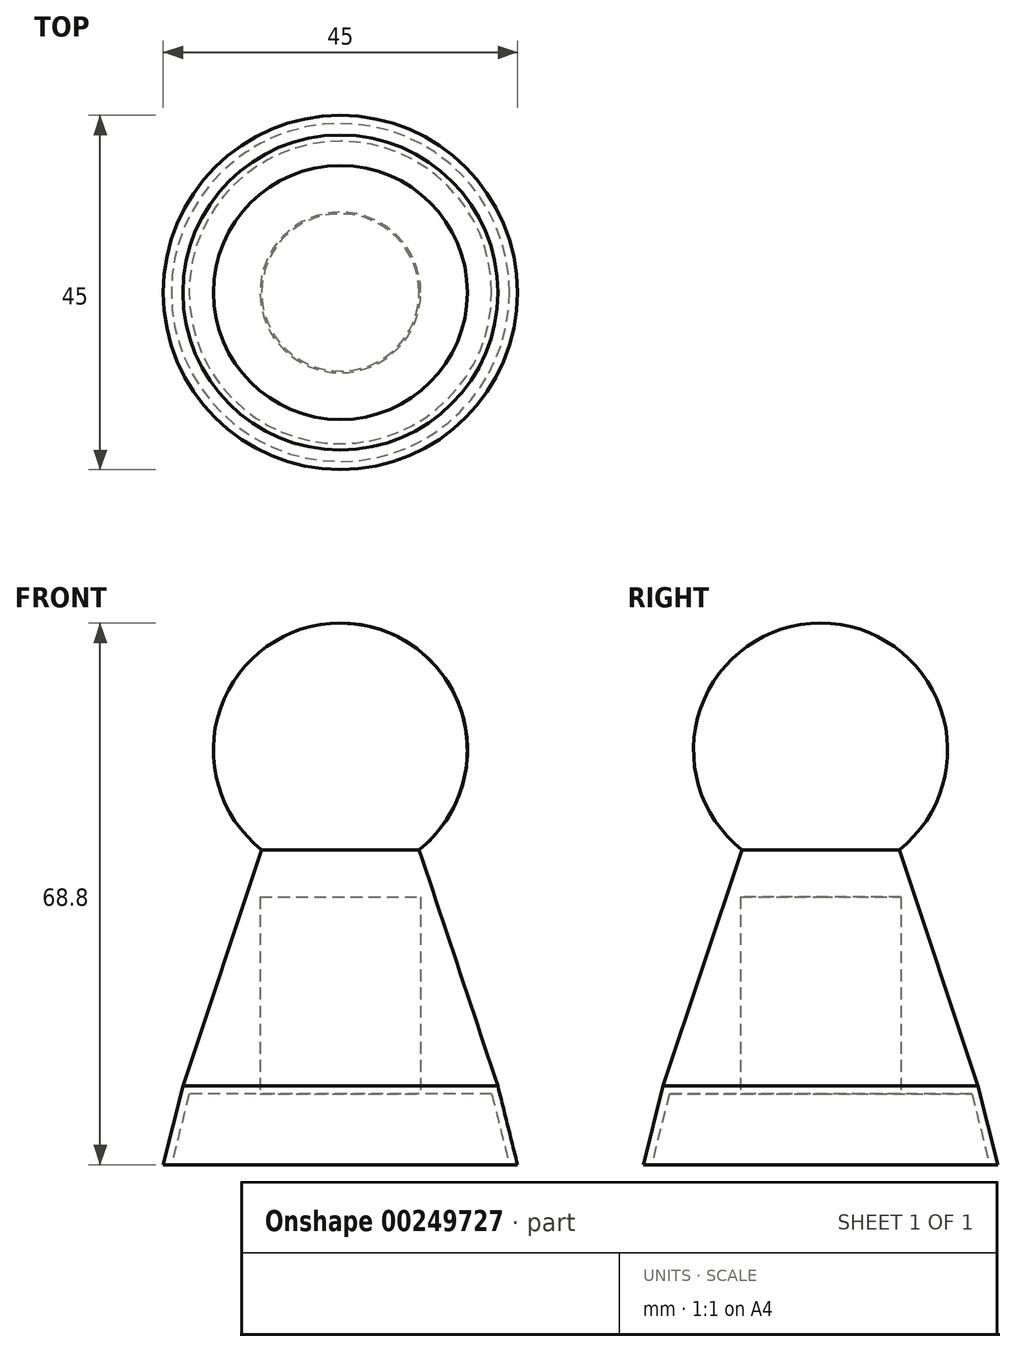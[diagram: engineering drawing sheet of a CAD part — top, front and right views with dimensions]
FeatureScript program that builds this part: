
annotation { "Feature Type Name" : "Feature", "Feature Type Description" : "" }
export const myFeature = defineFeature(function(context is Context, id is Id, definition is map)
    precondition{}
    {
        {
            var Q0;
            Q0=qCreatedBy(makeId("Top.planeOp"),FACE);
            var sketch = newSketch(context, id + "F0", { "sketchPlane" : qUnion([Q0])});
            skCircle(sketch, "E0", {"center": v(0, 0) * mm, "radius": 22.5 * mm});
            skSolve(sketch);
        }
        {
            var Q0;
            Q0=qCreatedBy(makeId("Top.planeOp"),FACE);
            cPlane(context, id + "F1", {"entities" : qUnion([Q0]), "cplaneType" : CPlaneType.OFFSET, "offset" : 10 * mm, "width" : 150 * mm, "height" : 150 * mm});
        }
        {
            var Q0;
            Q0=qCreatedBy(id+"F1.planeOp",FACE);
            var sketch = newSketch(context, id + "F2", { "sketchPlane" : qUnion([Q0])});
            skCircle(sketch, "E1", {"center": v(0, 0) * mm, "radius": 20 * mm});
            skSolve(sketch);
        }
        {
            var Q0;
            Q0=makeQuery(id+"F2.imprint","IMPRINT",FACE,{"disambiguationData":[TD([[makeQuery(id+"F2.imprint","IMPRINT",EDGE,{"derivedFrom":sQuery(id+"F2.wireOp",EDGE,"E1")}),1.0]])]});
            var Q1;
            Q1=makeQuery(id+"F0.imprint","IMPRINT",FACE,{"disambiguationData":[TD([[makeQuery(id+"F0.imprint","IMPRINT",EDGE,{"derivedFrom":sQuery(id+"F0.wireOp",EDGE,"E0")}),1.0]])]});
            loft(context, id + "F3", {"sheetProfilesArray" : [{ "sheetProfileEntities" : qUnion([Q0]) }, { "sheetProfileEntities" : qUnion([Q1]) }]});
        }
        {
            var Q0;
            Q0=makeQuery(id+"F3.opLoft","CAP_FACE",FACE,{"disambiguationData":[OSD([makeQuery(id+"F0.imprint","IMPRINT",FACE,{"disambiguationData":[TD([[makeQuery(id+"F0.imprint","IMPRINT",EDGE,{"derivedFrom":sQuery(id+"F0.wireOp",EDGE,"E0")}),1.0]])]})])],"isStart":true});
            shell(context, id + "F4", {"entities" : qUnion([Q0]), "thickness" : 1 * mm});
        }
        {
            var Q0;
            Q0=makeQuery(id+"F3.opLoft","CAP_FACE",FACE,{"disambiguationData":[OSD([makeQuery(id+"F2.imprint","IMPRINT",FACE,{"disambiguationData":[TD([[makeQuery(id+"F2.imprint","IMPRINT",EDGE,{"derivedFrom":sQuery(id+"F2.wireOp",EDGE,"E1")}),1.0]])]})])],"isStart":true});
            var sketch = newSketch(context, id + "F5", { "sketchPlane" : qUnion([Q0])});
            skSolve(sketch);
        }
        {
            var Q0;
            Q0=makeQuery(id+"F5.imprint","IMPRINT",FACE,{"disambiguationData":[TD([[makeQuery(id+"F5.imprint","IMPRINT",EDGE,{"derivedFrom":makeQuery(id+"F3.opLoft","MID_CAP_EDGE",EDGE,{"disambiguationData":[OSD([sQuery(id+"F2.wireOp",EDGE,"E1")])],"capPos":0.0})}),-1.0]])]});
            cPlane(context, id + "F6", {"entities" : qUnion([Q0]), "cplaneType" : CPlaneType.OFFSET, "offset" : 30 * mm, "width" : 150 * mm, "height" : 150 * mm});
        }
        {
            var Q0;
            Q0=qCreatedBy(id+"F6.planeOp",FACE);
            var sketch = newSketch(context, id + "F7", { "sketchPlane" : qUnion([Q0])});
            skCircle(sketch, "E2", {"center": v(0, 0) * mm, "radius": 10 * mm});
            skSolve(sketch);
        }
        {
            var Q1;
            Q1=makeQuery(id+"F5.imprint","IMPRINT",FACE,{"disambiguationData":[TD([[makeQuery(id+"F5.imprint","IMPRINT",EDGE,{"derivedFrom":makeQuery(id+"F3.opLoft","MID_CAP_EDGE",EDGE,{"disambiguationData":[OSD([sQuery(id+"F2.wireOp",EDGE,"E1")])],"capPos":0.0})}),-1.0]])]});
            var Q2;
            Q2=makeQuery(id+"F7.imprint","IMPRINT",FACE,{"disambiguationData":[TD([[makeQuery(id+"F7.imprint","IMPRINT",EDGE,{"derivedFrom":sQuery(id+"F7.wireOp",EDGE,"E2")}),1.0]])]});
            loft(context, id + "F8", {"operationType" : NewBodyOperationType.ADD, "sheetProfilesArray" : [{ "sheetProfileEntities" : qUnion([Q1]) }, { "sheetProfileEntities" : qUnion([Q2]) }]});
        }
        {
            var Q0;
            Q0=makeQuery(id+"F4.opShell","OFFSET_FACE",FACE,{"disambiguationData":[OSD([makeQuery(id+"F2.imprint","IMPRINT",FACE,{"disambiguationData":[TD([[makeQuery(id+"F2.imprint","IMPRINT",EDGE,{"derivedFrom":sQuery(id+"F2.wireOp",EDGE,"E1")}),1.0]])]})])]});
            var sketch = newSketch(context, id + "F9", { "sketchPlane" : qUnion([Q0])});
            skCircle(sketch, "E3.0.0", {"center": v(0, 0) * mm, "radius": 19.22 * mm, "construction": true});
            skCircle(sketch, "E4", {"center": v(0, 0) * mm, "radius": 10.2 * mm});
            skSolve(sketch);
        }
        {
            var Q0;
            Q0=makeQuery(id+"F9.imprint","IMPRINT",FACE,{"disambiguationData":[TD([[makeQuery(id+"F9.imprint","IMPRINT",EDGE,{"derivedFrom":sQuery(id+"F9.wireOp",EDGE,"E4")}),1.0]])]});
            extrude(context, id + "F10", {"entities" : qUnion([Q0]), "operationType" : NewBodyOperationType.REMOVE, "oppositeDirection" : true, "depth" : 25 * mm});
        }
        {
            var Q0;
            Q0=qCreatedBy(makeId("Front.planeOp"),FACE);
            var sketch = newSketch(context, id + "F11", { "sketchPlane" : qUnion([Q0])});
            skLineSegment(sketch, "E5.0", {"start": v(-10, 40) * mm, "end": v(10, 40) * mm});
            skLineSegment(sketch, "E6", {"start": v(0, 73.64) * mm, "end": v(0, 40) * mm});
            skArc(sketch, "E7", {"start": v(10, 40) * mm, "mid": v(15.24, 57.96) * mm, "end": v(0, 68.8) * mm});
            skSolve(sketch);
        }
        {
            var Q0;
            Q0 = qSketchRegion(id + "F11", true);
            var Q1;
            Q1=sQuery(id+"F11.wireOp",EDGE,"E6");
            revolve(context, id + "F12", {"operationType" : NewBodyOperationType.ADD, "entities" : qUnion([Q0]), "axis" : qUnion([Q1]), "revolveType" : RevolveType.FULL});
        }
    });
